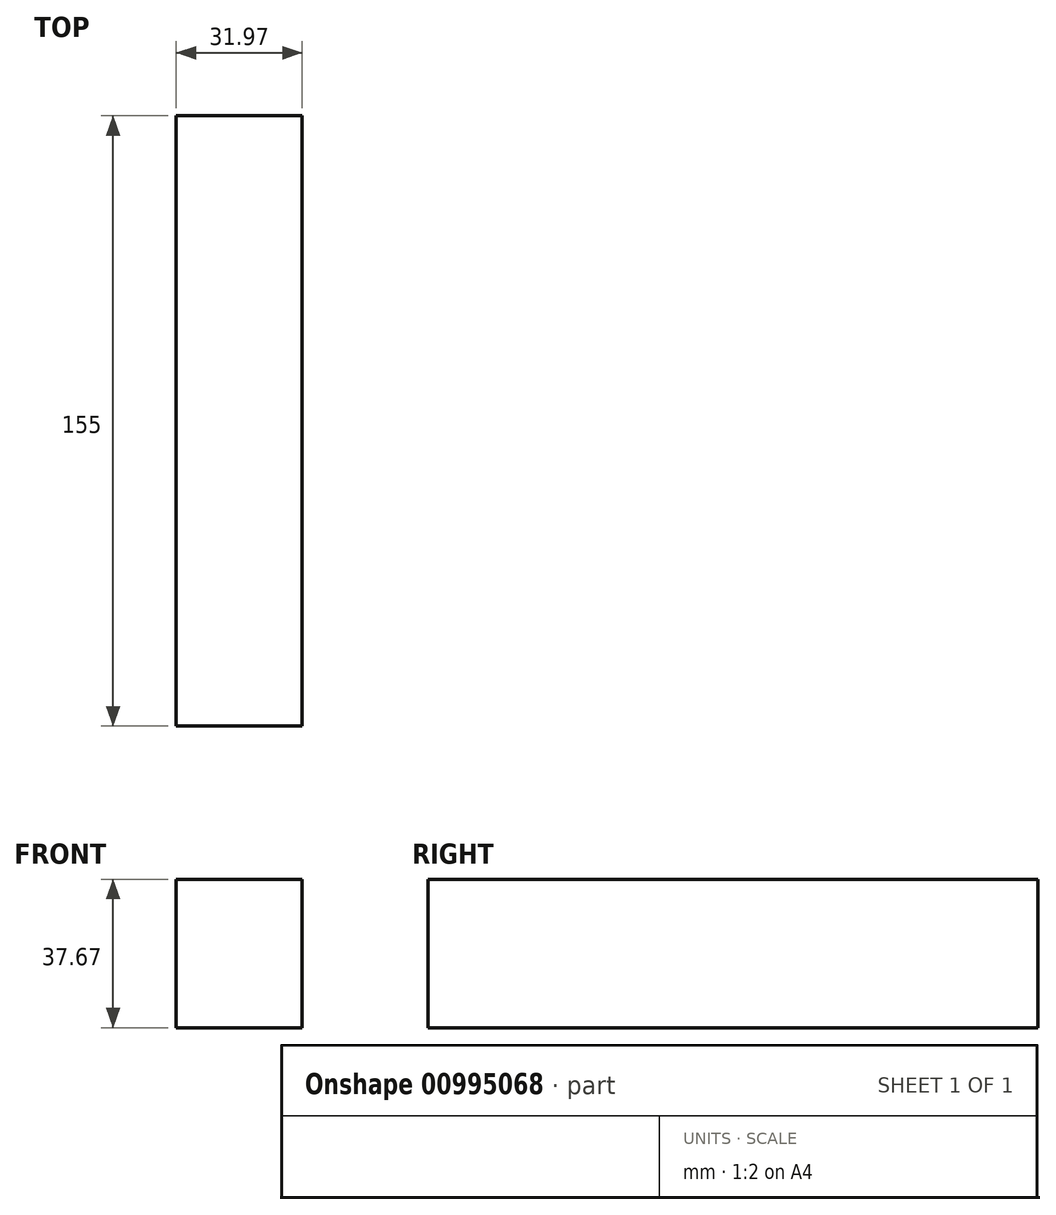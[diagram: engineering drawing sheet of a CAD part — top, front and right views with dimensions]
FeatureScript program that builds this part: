
annotation { "Feature Type Name" : "Feature", "Feature Type Description" : "" }
export const myFeature = defineFeature(function(context is Context, id is Id, definition is map)
    precondition{}
    {
        {
            var Q0;
            Q0=qCreatedBy(makeId("Front.planeOp"),FACE);
            var sketch = newSketch(context, id + "F0", { "sketchPlane" : qUnion([Q0])});
            skLineSegment(sketch, "E0.bottom", {"start": v(0, 0) * mm, "end": v(31.97, 0) * mm});
            skLineSegment(sketch, "E0.top", {"start": v(0, -37.67) * mm, "end": v(31.97, -37.67) * mm});
            skLineSegment(sketch, "E0.left", {"start": v(0, 0) * mm, "end": v(0, -37.67) * mm});
            skLineSegment(sketch, "E0.right", {"start": v(31.97, 0) * mm, "end": v(31.97, -37.67) * mm});
            skSolve(sketch);
        }
        {
            var Q0;
            Q0=makeQuery(id+"F0.imprint","IMPRINT",FACE,{"disambiguationData":[TD([[makeQuery(id+"F0.imprint","IMPRINT",EDGE,{"derivedFrom":sQuery(id+"F0.wireOp",EDGE,"E0.bottom")}),-1.0]])]});
            extrude(context, id + "F1", {"entities" : qUnion([Q0]), "depth" : 155 * mm, "offsetDistance" : 25 * mm});
        }
    });
